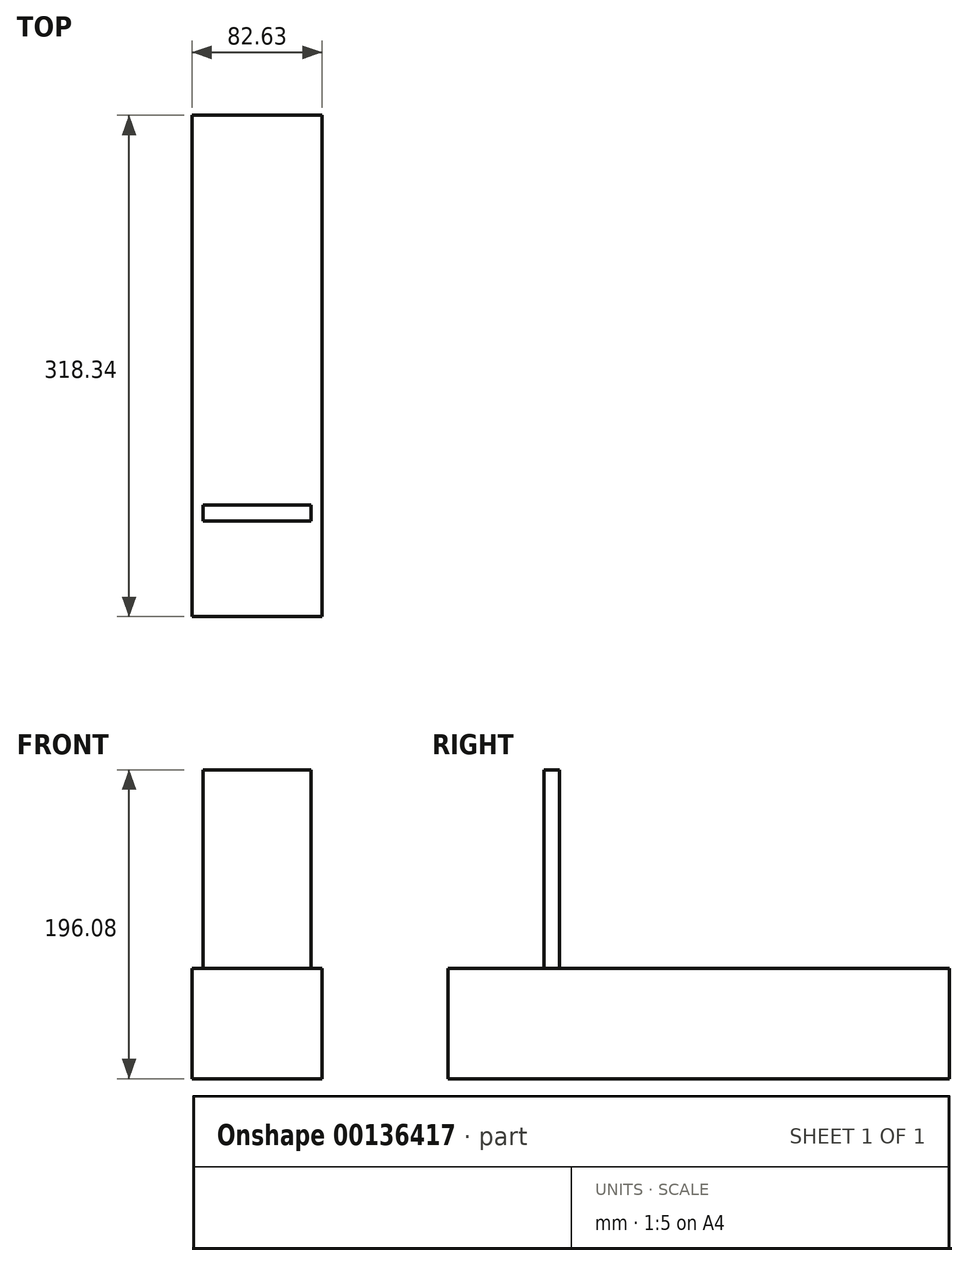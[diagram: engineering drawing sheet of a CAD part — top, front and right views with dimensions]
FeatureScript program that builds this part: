
annotation { "Feature Type Name" : "Feature", "Feature Type Description" : "" }
export const myFeature = defineFeature(function(context is Context, id is Id, definition is map)
    precondition{}
    {
        {
            var Q0;
            Q0=qCreatedBy(makeId("Front.planeOp"),FACE);
            var sketch = newSketch(context, id + "F0", { "sketchPlane" : qUnion([Q0])});
            skLineSegment(sketch, "E0.bottom", {"start": v(-37.39, 34.85) * mm, "end": v(45.24, 34.85) * mm});
            skLineSegment(sketch, "E0.top", {"start": v(-37.39, -35.31) * mm, "end": v(45.24, -35.31) * mm});
            skLineSegment(sketch, "E0.left", {"start": v(-37.39, 34.85) * mm, "end": v(-37.39, -35.31) * mm});
            skLineSegment(sketch, "E0.right", {"start": v(45.24, 34.85) * mm, "end": v(45.24, -35.31) * mm});
            skSolve(sketch);
        }
        {
            var Q0;
            Q0=makeQuery(id+"F0.imprint","IMPRINT",FACE,{"disambiguationData":[TD([[makeQuery(id+"F0.imprint","IMPRINT",EDGE,{"derivedFrom":sQuery(id+"F0.wireOp",EDGE,"E0.bottom")}),-1.0]])]});
            extrude(context, id + "F1", {"entities" : qUnion([Q0]), "depth" : 318.34 * mm});
        }
        {
            var Q0;
            Q0=qCreatedBy(makeId("Top.planeOp"),FACE);
            var sketch = newSketch(context, id + "F2", { "sketchPlane" : qUnion([Q0])});
            skLineSegment(sketch, "E1.bottom", {"start": v(-30.47, -257.61) * mm, "end": v(38.19, -257.61) * mm});
            skLineSegment(sketch, "E1.top", {"start": v(-30.47, -247.58) * mm, "end": v(38.19, -247.58) * mm});
            skLineSegment(sketch, "E1.left", {"start": v(-30.47, -257.61) * mm, "end": v(-30.47, -247.58) * mm});
            skLineSegment(sketch, "E1.right", {"start": v(38.19, -257.61) * mm, "end": v(38.19, -247.58) * mm});
            skSolve(sketch);
        }
        {
            var Q0;
            Q0 = qSketchRegion(id + "F2", true);
            extrude(context, id + "F3", {"entities" : qUnion([Q0]), "operationType" : NewBodyOperationType.ADD, "depth" : 160.77 * mm});
        }
    });
